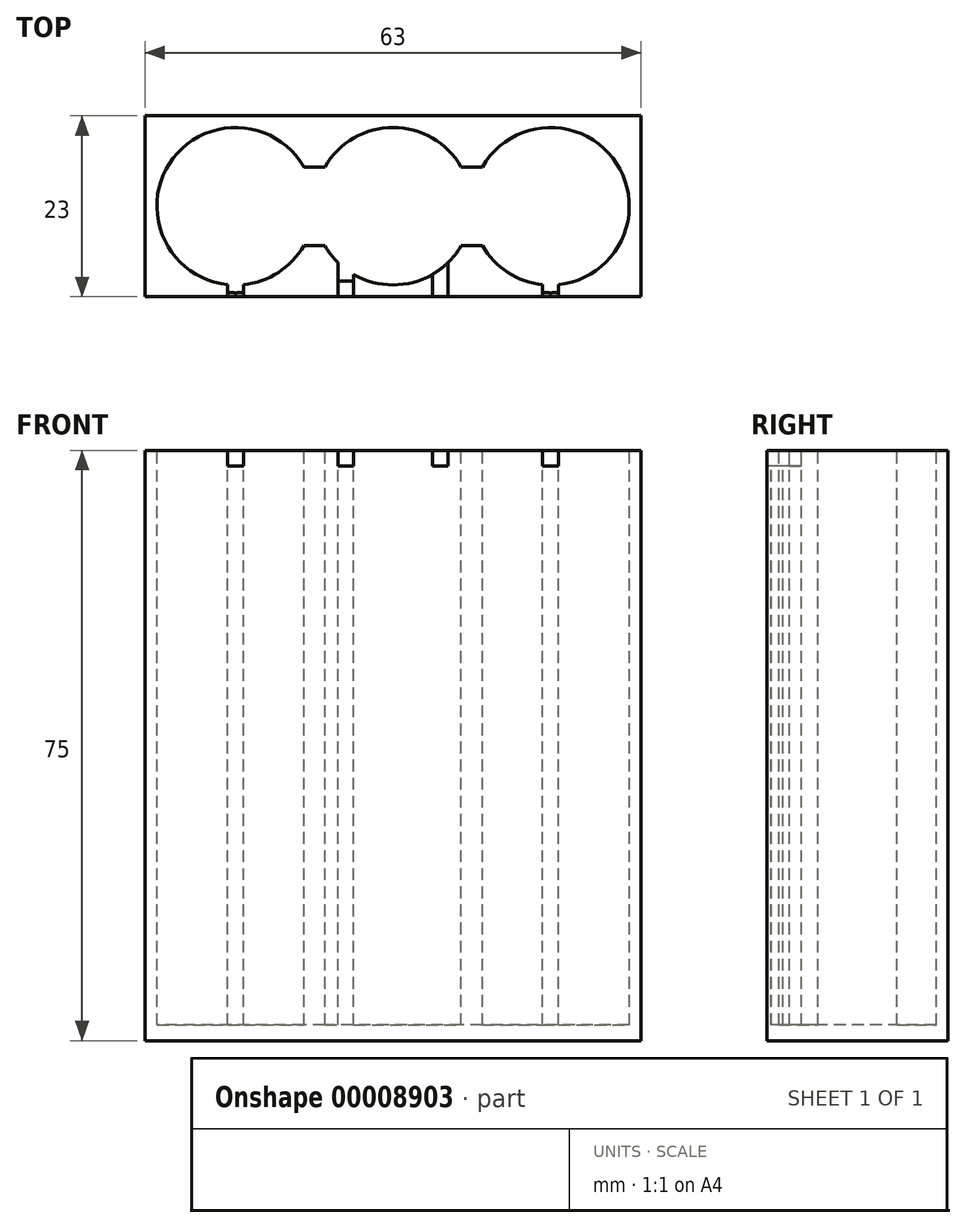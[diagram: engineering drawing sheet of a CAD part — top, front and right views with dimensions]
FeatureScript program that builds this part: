
annotation { "Feature Type Name" : "Feature", "Feature Type Description" : "" }
export const myFeature = defineFeature(function(context is Context, id is Id, definition is map)
    precondition{}
    {
        {
            var Q0;
            Q0=qCreatedBy(makeId("Top.planeOp"),FACE);
            var sketch = newSketch(context, id + "F0", { "sketchPlane" : qUnion([Q0])});
            skLineSegment(sketch, "E0.0", {"start": v(0, 12) * mm, "end": v(-32, 12) * mm, "construction": true});
            skLineSegment(sketch, "E1.0", {"start": v(0, 12) * mm, "end": v(32, 12) * mm, "construction": true});
            skLineSegment(sketch, "E2.0", {"start": v(0, -12) * mm, "end": v(-32, -12) * mm, "construction": true});
            skLineSegment(sketch, "E3.0", {"start": v(0, -12) * mm, "end": v(32, -12) * mm, "construction": true});
            skLineSegment(sketch, "E4", {"start": v(-32, 12) * mm, "end": v(-32, -12) * mm, "construction": true});
            skLineSegment(sketch, "E5", {"start": v(32, 12) * mm, "end": v(32, -12) * mm, "construction": true});
            skCircle(sketch, "E6", {"center": v(0, 0) * mm, "radius": 10 * mm});
            skLineSegment(sketch, "E7", {"start": v(0, 0) * mm, "end": v(-20, 0) * mm, "construction": true});
            skLineSegment(sketch, "E8", {"start": v(0, 0) * mm, "end": v(20, 0) * mm, "construction": true});
            skCircle(sketch, "E9", {"center": v(-20, 0) * mm, "radius": 10 * mm});
            skCircle(sketch, "E10", {"center": v(20, 0) * mm, "radius": 10 * mm});
            skLineSegment(sketch, "E11.0", {"start": v(-31.5, 12) * mm, "end": v(-31.5, -12) * mm});
            skLineSegment(sketch, "E12.0", {"start": v(31.5, 12) * mm, "end": v(31.5, -12) * mm});
            skLineSegment(sketch, "E13.0", {"start": v(0, 11.5) * mm, "end": v(32, 11.5) * mm});
            skLineSegment(sketch, "E14.0", {"start": v(0, 11.5) * mm, "end": v(-32, 11.5) * mm});
            skLineSegment(sketch, "E15.0", {"start": v(0, -11.5) * mm, "end": v(32, -11.5) * mm});
            skLineSegment(sketch, "E16.0", {"start": v(0, -11.5) * mm, "end": v(-32, -11.5) * mm});
            skLineSegment(sketch, "E17.0", {"start": v(32, -5) * mm, "end": v(31.5, -5) * mm});
            skLineSegment(sketch, "E18.trimOffspring", {"start": v(-31.5, 5) * mm, "end": v(-32, 5) * mm});
            skLineSegment(sketch, "E19.trimOffspring", {"start": v(-8.66, -5) * mm, "end": v(-11.34, -5) * mm});
            skLineSegment(sketch, "E20.trimOffspring", {"start": v(-8.66, 5) * mm, "end": v(-11.34, 5) * mm});
            skLineSegment(sketch, "E21.trimOffspring", {"start": v(11.34, 5) * mm, "end": v(8.66, 5) * mm});
            skLineSegment(sketch, "E22.trimOffspring", {"start": v(11.34, -5) * mm, "end": v(8.66, -5) * mm});
            skSolve(sketch);
        }
        {
            var Q0;
            {var subQ13=sQuery(id+"F0.wireOp",EDGE,"E19.trimOffspring");Q0=makeQuery(id+"F0.imprint","IMPRINT",FACE,{"disambiguationData":[TD([[makeQuery(id+"F0.imprint","IMPRINT",EDGE,{"derivedFrom":subQ13}),1.0]])]});}
            var Q1;
            {var subQ0=sQuery(id+"F0.wireOp",EDGE,"E9");var subQ3=makeQuery(id+"F0.imprint","INTERSECT",VERTEX,{"derivedFrom":[subQ0,sQuery(id+"F0.wireOp",EDGE,"E20.trimOffspring")]});Q1=makeQuery(id+"F0.imprint","IMPRINT",FACE,{"disambiguationData":[TD([[makeQuery(id+"F0.imprint","IMPRINT",EDGE,{"disambiguationData":[TD([[subQ3,1.0]])],"derivedFrom":subQ0}),1.0]])]});}
            var Q2;
            {var subQ0=sQuery(id+"F0.wireOp",EDGE,"E19.trimOffspring");Q2=makeQuery(id+"F0.imprint","IMPRINT",FACE,{"disambiguationData":[TD([[makeQuery(id+"F0.imprint","IMPRINT",EDGE,{"derivedFrom":subQ0}),-1.0]])]});}
            var Q3;
            {var subQ0=sQuery(id+"F0.wireOp",EDGE,"E6");var subQ6=makeQuery(id+"F0.imprint","INTERSECT",VERTEX,{"derivedFrom":[subQ0,sQuery(id+"F0.wireOp",EDGE,"E21.trimOffspring")]});Q3=makeQuery(id+"F0.imprint","IMPRINT",FACE,{"disambiguationData":[TD([[makeQuery(id+"F0.imprint","IMPRINT",EDGE,{"disambiguationData":[TD([[subQ6,1.0]])],"derivedFrom":subQ0}),1.0]])]});}
            var Q4;
            {var subQ0=sQuery(id+"F0.wireOp",EDGE,"E20.trimOffspring");Q4=makeQuery(id+"F0.imprint","IMPRINT",FACE,{"disambiguationData":[TD([[makeQuery(id+"F0.imprint","IMPRINT",EDGE,{"derivedFrom":subQ0}),1.0]])]});}
            var Q5;
            {var subQ0=sQuery(id+"F0.wireOp",EDGE,"E21.trimOffspring");Q5=makeQuery(id+"F0.imprint","IMPRINT",FACE,{"disambiguationData":[TD([[makeQuery(id+"F0.imprint","IMPRINT",EDGE,{"derivedFrom":subQ0}),1.0]])]});}
            var Q6;
            {var subQ0=sQuery(id+"F0.wireOp",EDGE,"E22.trimOffspring");Q6=makeQuery(id+"F0.imprint","IMPRINT",FACE,{"disambiguationData":[TD([[makeQuery(id+"F0.imprint","IMPRINT",EDGE,{"derivedFrom":subQ0}),-1.0]])]});}
            var Q7;
            {var subQ0=sQuery(id+"F0.wireOp",EDGE,"E10");var subQ2=makeQuery(id+"F0.imprint","INTERSECT",VERTEX,{"derivedFrom":[subQ0,sQuery(id+"F0.wireOp",EDGE,"E21.trimOffspring")]});Q7=makeQuery(id+"F0.imprint","IMPRINT",FACE,{"disambiguationData":[TD([[makeQuery(id+"F0.imprint","IMPRINT",EDGE,{"disambiguationData":[TD([[subQ2,-1.0]])],"derivedFrom":subQ0}),1.0]])]});}
            extrude(context, id + "F1", {"entities" : qUnion([Q0, Q1, Q2, Q3, Q4, Q5, Q6, Q7]), "oppositeDirection" : true, "depth" : 75 * mm});
        }
        {
            var Q0;
            {var subQ0=sQuery(id+"F0.wireOp",EDGE,"E9");var subQ3=makeQuery(id+"F0.imprint","INTERSECT",VERTEX,{"derivedFrom":[subQ0,sQuery(id+"F0.wireOp",EDGE,"E20.trimOffspring")]});Q0=makeQuery(id+"F0.imprint","IMPRINT",FACE,{"disambiguationData":[TD([[makeQuery(id+"F0.imprint","IMPRINT",EDGE,{"disambiguationData":[TD([[subQ3,1.0]])],"derivedFrom":subQ0}),1.0]])]});}
            var Q1;
            {var subQ0=sQuery(id+"F0.wireOp",EDGE,"E19.trimOffspring");Q1=makeQuery(id+"F0.imprint","IMPRINT",FACE,{"disambiguationData":[TD([[makeQuery(id+"F0.imprint","IMPRINT",EDGE,{"derivedFrom":subQ0}),-1.0]])]});}
            var Q2;
            {var subQ0=sQuery(id+"F0.wireOp",EDGE,"E20.trimOffspring");Q2=makeQuery(id+"F0.imprint","IMPRINT",FACE,{"disambiguationData":[TD([[makeQuery(id+"F0.imprint","IMPRINT",EDGE,{"derivedFrom":subQ0}),1.0]])]});}
            var Q3;
            {var subQ0=sQuery(id+"F0.wireOp",EDGE,"E6");var subQ6=makeQuery(id+"F0.imprint","INTERSECT",VERTEX,{"derivedFrom":[subQ0,sQuery(id+"F0.wireOp",EDGE,"E21.trimOffspring")]});Q3=makeQuery(id+"F0.imprint","IMPRINT",FACE,{"disambiguationData":[TD([[makeQuery(id+"F0.imprint","IMPRINT",EDGE,{"disambiguationData":[TD([[subQ6,1.0]])],"derivedFrom":subQ0}),1.0]])]});}
            var Q4;
            {var subQ0=sQuery(id+"F0.wireOp",EDGE,"E21.trimOffspring");Q4=makeQuery(id+"F0.imprint","IMPRINT",FACE,{"disambiguationData":[TD([[makeQuery(id+"F0.imprint","IMPRINT",EDGE,{"derivedFrom":subQ0}),1.0]])]});}
            var Q5;
            {var subQ0=sQuery(id+"F0.wireOp",EDGE,"E22.trimOffspring");Q5=makeQuery(id+"F0.imprint","IMPRINT",FACE,{"disambiguationData":[TD([[makeQuery(id+"F0.imprint","IMPRINT",EDGE,{"derivedFrom":subQ0}),-1.0]])]});}
            var Q6;
            {var subQ0=sQuery(id+"F0.wireOp",EDGE,"E10");var subQ2=makeQuery(id+"F0.imprint","INTERSECT",VERTEX,{"derivedFrom":[subQ0,sQuery(id+"F0.wireOp",EDGE,"E21.trimOffspring")]});Q6=makeQuery(id+"F0.imprint","IMPRINT",FACE,{"disambiguationData":[TD([[makeQuery(id+"F0.imprint","IMPRINT",EDGE,{"disambiguationData":[TD([[subQ2,-1.0]])],"derivedFrom":subQ0}),1.0]])]});}
            extrude(context, id + "F2", {"entities" : qUnion([Q0, Q1, Q2, Q3, Q4, Q5, Q6]), "operationType" : NewBodyOperationType.REMOVE, "oppositeDirection" : true, "depth" : 73 * mm});
        }
        {
            var Q0;
            {var subQ13=sQuery(id+"F0.wireOp",EDGE,"E19.trimOffspring");Q0=makeQuery(id+"F0.imprint","IMPRINT",FACE,{"disambiguationData":[TD([[makeQuery(id+"F0.imprint","IMPRINT",EDGE,{"derivedFrom":subQ13}),1.0]])]});}
            var sketch = newSketch(context, id + "F3", { "sketchPlane" : qUnion([Q0])});
            skLineSegment(sketch, "E23", {"start": v(0, -11.5) * mm, "end": v(0, -15.75) * mm});
            skLineSegment(sketch, "E24.0", {"start": v(0, -11.5) * mm, "end": v(-32, -11.5) * mm});
            skLineSegment(sketch, "E25.0", {"start": v(-5, -7.86) * mm, "end": v(-5, -15.75) * mm});
            skLineSegment(sketch, "E26.0", {"start": v(5, -8.3) * mm, "end": v(5, -15.75) * mm});
            skLineSegment(sketch, "E27.0", {"start": v(-7, -6.45) * mm, "end": v(-7, -15.75) * mm});
            skLineSegment(sketch, "E28.0", {"start": v(7, -7.05) * mm, "end": v(7, -15.75) * mm});
            skLineSegment(sketch, "E29", {"start": v(0, -11.5) * mm, "end": v(32.18, -11.5) * mm});
            skArc(sketch, "E30.0", {"start": v(-7, -7.14) * mm, "mid": v(0, -10) * mm, "end": v(7, -7.14) * mm});
            skLineSegment(sketch, "E31.0", {"start": v(-20, -5.64) * mm, "end": v(-20, -15.75) * mm, "construction": true});
            skLineSegment(sketch, "E32.0", {"start": v(20, -7.5) * mm, "end": v(20, -15.75) * mm, "construction": true});
            skLineSegment(sketch, "E33.0", {"start": v(-21, -8.57) * mm, "end": v(-21, -15.75) * mm});
            skLineSegment(sketch, "E34.0", {"start": v(-19, -7.04) * mm, "end": v(-19, -15.75) * mm});
            skLineSegment(sketch, "E35.0", {"start": v(19, -8.5) * mm, "end": v(19, -15.75) * mm});
            skLineSegment(sketch, "E36.0", {"start": v(21, -5.9) * mm, "end": v(21, -15.75) * mm});
            skArc(sketch, "E37.0", {"start": v(-11.34, 5) * mm, "mid": v(-30, 0) * mm, "end": v(-11.34, -5) * mm});
            skArc(sketch, "E38.0", {"start": v(11.34, -5) * mm, "mid": v(30, 0) * mm, "end": v(11.34, 5) * mm});
            skSolve(sketch);
        }
        {
            var Q0;
            {var subQ1=sQuery(id+"F3.wireOp",EDGE,"E25.0");var subQ6=sQuery(id+"F3.wireOp",EDGE,"E24.0");var subQ8=makeQuery(id+"F3.imprint","INTERSECT",VERTEX,{"derivedFrom":[subQ6,subQ1]});Q0=makeQuery(id+"F3.imprint","IMPRINT",FACE,{"disambiguationData":[TD([[makeQuery(id+"F3.imprint","IMPRINT",EDGE,{"disambiguationData":[TD([[subQ8,-1.0]])],"derivedFrom":subQ6}),-1.0]])]});}
            var Q1;
            {var subQ1=sQuery(id+"F3.wireOp",EDGE,"E26.0");var subQ6=sQuery(id+"F3.wireOp",EDGE,"E29");var subQ7=makeQuery(id+"F3.imprint","INTERSECT",VERTEX,{"derivedFrom":[subQ1,subQ6]});Q1=makeQuery(id+"F3.imprint","IMPRINT",FACE,{"disambiguationData":[TD([[makeQuery(id+"F3.imprint","IMPRINT",EDGE,{"disambiguationData":[TD([[subQ7,1.0]])],"derivedFrom":subQ1}),1.0]])]});}
            var Q2;
            {var subQ1=sQuery(id+"F3.wireOp",EDGE,"E34.0");var subQ5=sQuery(id+"F3.wireOp",EDGE,"E24.0");var subQ6=makeQuery(id+"F3.imprint","INTERSECT",VERTEX,{"derivedFrom":[subQ5,subQ1]});Q2=makeQuery(id+"F3.imprint","IMPRINT",FACE,{"disambiguationData":[TD([[makeQuery(id+"F3.imprint","IMPRINT",EDGE,{"disambiguationData":[TD([[subQ6,-1.0]])],"derivedFrom":subQ5}),-1.0]])]});}
            var Q3;
            {var subQ3=sQuery(id+"F3.wireOp",EDGE,"E35.0");var subQ5=sQuery(id+"F3.wireOp",EDGE,"E29");var subQ7=makeQuery(id+"F3.imprint","INTERSECT",VERTEX,{"derivedFrom":[subQ5,subQ3]});Q3=makeQuery(id+"F3.imprint","IMPRINT",FACE,{"disambiguationData":[TD([[makeQuery(id+"F3.imprint","IMPRINT",EDGE,{"disambiguationData":[TD([[subQ7,-1.0]])],"derivedFrom":subQ5}),1.0]])]});}
            extrude(context, id + "F4", {"entities" : qUnion([Q0, Q1, Q2, Q3]), "operationType" : NewBodyOperationType.REMOVE, "oppositeDirection" : true, "depth" : 2 * mm});
        }
        {
            var Q0;
            Q0=makeQuery(id+"F4.boolean.opBoolean","COPY",FACE,{"derivedFrom":makeQuery(id+"F4.opExtrude","CAP_FACE",FACE,{"disambiguationData":[OSD([sQuery(id+"F3.wireOp",EDGE,"E24.0"),sQuery(id+"F3.wireOp",EDGE,"E25.0"),sQuery(id+"F3.wireOp",EDGE,"E27.0"),sQuery(id+"F3.wireOp",EDGE,"E30.0")])],"isStart":false})});
            var sketch = newSketch(context, id + "F5", { "sketchPlane" : qUnion([Q0])});
            skArc(sketch, "E39.0", {"start": v(-21.1, -10.94) * mm, "mid": v(-20, -11) * mm, "end": v(-18.9, -10.94) * mm});
            skLineSegment(sketch, "E40.0", {"start": v(-5, -9.5) * mm, "end": v(-7, -9.5) * mm});
            skArc(sketch, "E41.0", {"start": v(18.9, -10.94) * mm, "mid": v(20, -11) * mm, "end": v(21.1, -10.94) * mm});
            skArc(sketch, "E42.0", {"start": v(-21, -9.95) * mm, "mid": v(-20, -10) * mm, "end": v(-19, -9.95) * mm});
            skLineSegment(sketch, "E43", {"start": v(-19, -9.95) * mm, "end": v(-19, -11.48) * mm});
            skArc(sketch, "E44.0", {"start": v(19, -9.95) * mm, "mid": v(20, -10) * mm, "end": v(21, -9.95) * mm});
            skLineSegment(sketch, "E45", {"start": v(19, -9.95) * mm, "end": v(19, -11.5) * mm});
            skLineSegment(sketch, "E46", {"start": v(21, -9.95) * mm, "end": v(21, -11.52) * mm});
            skLineSegment(sketch, "E47", {"start": v(-21, -9.95) * mm, "end": v(-21, -11.52) * mm});
            skSolve(sketch);
        }
        {
            var Q0;
            {var subQ3=sQuery(id+"F5.wireOp",EDGE,"E42.0");Q0=makeQuery(id+"F5.imprint","IMPRINT",FACE,{"disambiguationData":[TD([[makeQuery(id+"F5.imprint","IMPRINT",EDGE,{"derivedFrom":subQ3}),-1.0]])]});}
            var Q1;
            {var subQ2=sQuery(id+"F5.wireOp",EDGE,"E40.0");Q1=makeQuery(id+"F5.imprint","IMPRINT",FACE,{"disambiguationData":[TD([[makeQuery(id+"F5.imprint","IMPRINT",EDGE,{"derivedFrom":subQ2}),-1.0]])]});}
            var Q2;
            {var subQ3=sQuery(id+"F5.wireOp",EDGE,"E44.0");Q2=makeQuery(id+"F5.imprint","IMPRINT",FACE,{"disambiguationData":[TD([[makeQuery(id+"F5.imprint","IMPRINT",EDGE,{"derivedFrom":subQ3}),-1.0]])]});}
            extrude(context, id + "F6", {"entities" : qUnion([Q0, Q1, Q2]), "operationType" : NewBodyOperationType.REMOVE, "oppositeDirection" : true, "depth" : 71 * mm});
        }
    });
